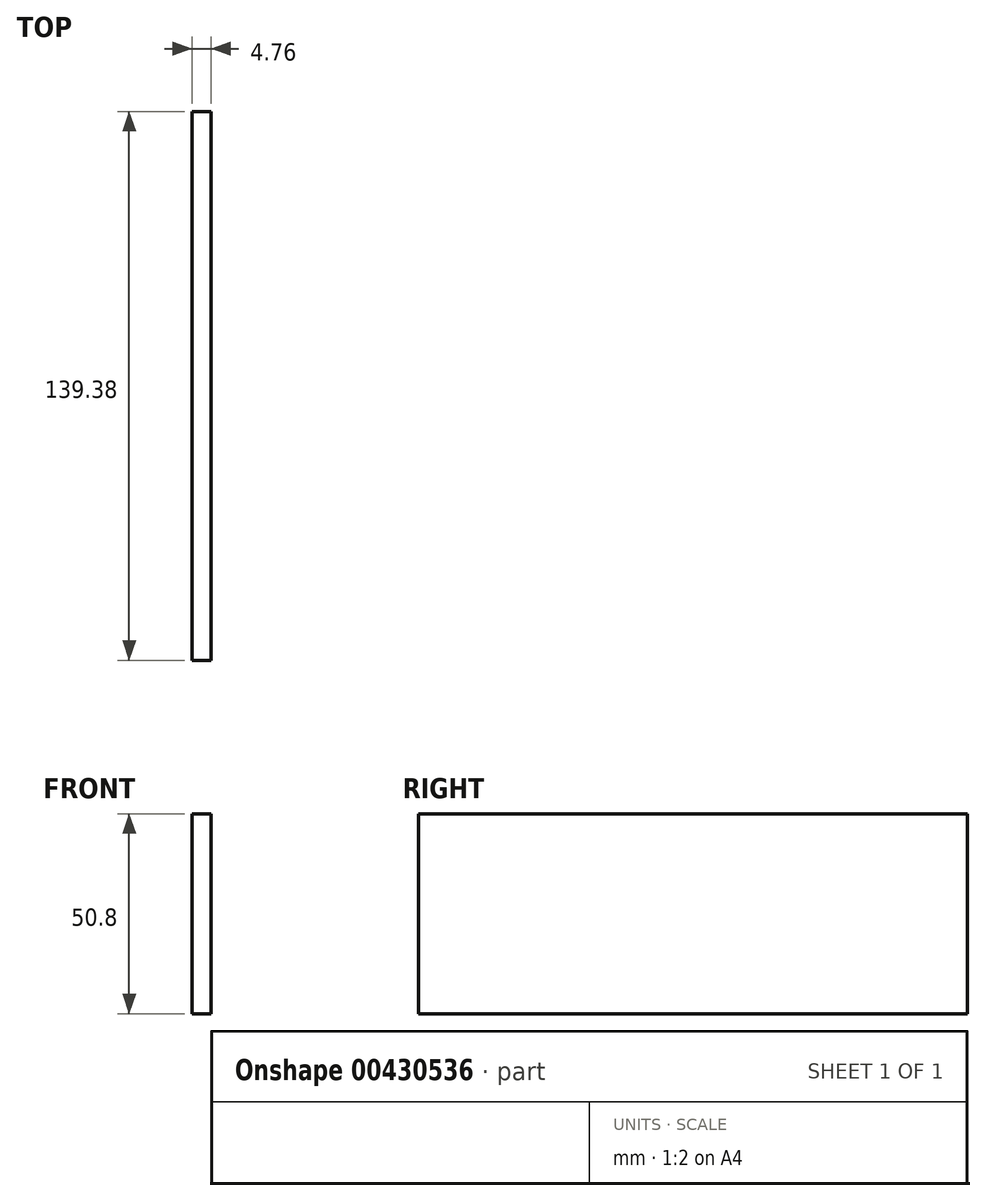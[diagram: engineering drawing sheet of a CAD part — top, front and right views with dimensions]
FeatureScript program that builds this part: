
annotation { "Feature Type Name" : "Feature", "Feature Type Description" : "" }
export const myFeature = defineFeature(function(context is Context, id is Id, definition is map)
    precondition{}
    {
        {
            var Q0;
            Q0=qCreatedBy(makeId("Right.planeOp"),FACE);
            var sketch = newSketch(context, id + "F0", { "sketchPlane" : qUnion([Q0])});
            skLineSegment(sketch, "E0.bottom", {"start": v(-24.08, 3.77) * mm, "end": v(115.3, 3.77) * mm});
            skLineSegment(sketch, "E0.top", {"start": v(-24.08, -47.03) * mm, "end": v(115.3, -47.03) * mm});
            skLineSegment(sketch, "E0.left", {"start": v(-24.08, 3.77) * mm, "end": v(-24.08, -47.03) * mm});
            skLineSegment(sketch, "E0.right", {"start": v(115.3, 3.77) * mm, "end": v(115.3, -47.03) * mm});
            skSolve(sketch);
        }
        {
            var Q0;
            Q0=makeQuery(id+"F0.imprint","IMPRINT",FACE,{"disambiguationData":[TD([[makeQuery(id+"F0.imprint","IMPRINT",EDGE,{"derivedFrom":sQuery(id+"F0.wireOp",EDGE,"E0.bottom")}),-1.0]])]});
            extrude(context, id + "F1", {"entities" : qUnion([Q0]), "depth" : 4.76 * mm});
        }
    });
